# Revit family: Haworth_UniGroupToo_Panel_DoorSliding
name_source: partatom
category: Furniture Systems
revit_build: Autodesk Revit 2018 (Build: 20170223_1515(x64)
units: mm (PartAtom-declared; Revit-internal decimal feet)

## family parameters
Always vertical = Yes
Cut with Voids When Loaded = No
OmniClass Number = 23.40.70.14.64.21
OmniClass Title = Systems Furniture
Part Type = Normal
Room Calculation Point = No
Round Connector Dimension = Use Diameter
Shared = No
Work Plane-Based = No

## types (1)
- 36w 80h
    Actual Height = 80"
    Actual Width = 36"
    Arrow Height = 40"
    Assembly Code = E2020500
    Bottom Trim Width = 3/8"
    Caster Bottom Offset = 1/4"
    Caster Offset = 3 3/8"
    Caster Radius = 2"
    Caster Reveal Height = 15/16"
    Custom Size = No
    Description = Haworth - UniGroup Too - Panel - Door - Sliding
    Glass Finish = Haworth _ Glass _ Frosted
    Glaze Inset = 3/4"
    Glazed Trim Height = 4 1/4"
    Glazed Trim Inset = 3/128"
    Glazed Trim Sides = 2 3/4"
    Height = 80"
    Manufacturer = Haworth
    Max. Height = 80"
    Max. Width = 42"
    Min. Height = 64"
    Min. Width = 36"
    Model = Haworth - UniGroup Too - Panel - Door - Sliding
    Notch Depth = 1/2"
    Notch Width = 109/128"
    Offset Front = 4 3/8"
    Panel Depth = 1/2"
    Panel Height = 75 55/64"
    Pull Length = 3"
    Pull Location = 27 3/8"
    Raceway Panel Width = 36"
    Revision Number = 2
    Size = Verify Final Dim. w/ Haworth
    Slide Offset Left = 30"
    Slide Offset Right = 4"
    Slide Rail Height = 29/64"
    Standard Heights = 64, 72, 80 inches
    Standard Widths = 36, 42 inches
    Sustainability Info = http://www.haworth.com
    Top Trim Height = 2 3/4"
    Trim Depth = 2"
    Trim Finish = Haworth _ Metal _ Brushed Aluminum
    URL = www.haworth.com
    URL - Product = http://www.haworth.com
    Warranty = http://www.haworth.com
    Width = 36"

## geometry (parser evidence)
native form markers: Sweep x3
no freeform markers — native parametric forms only
